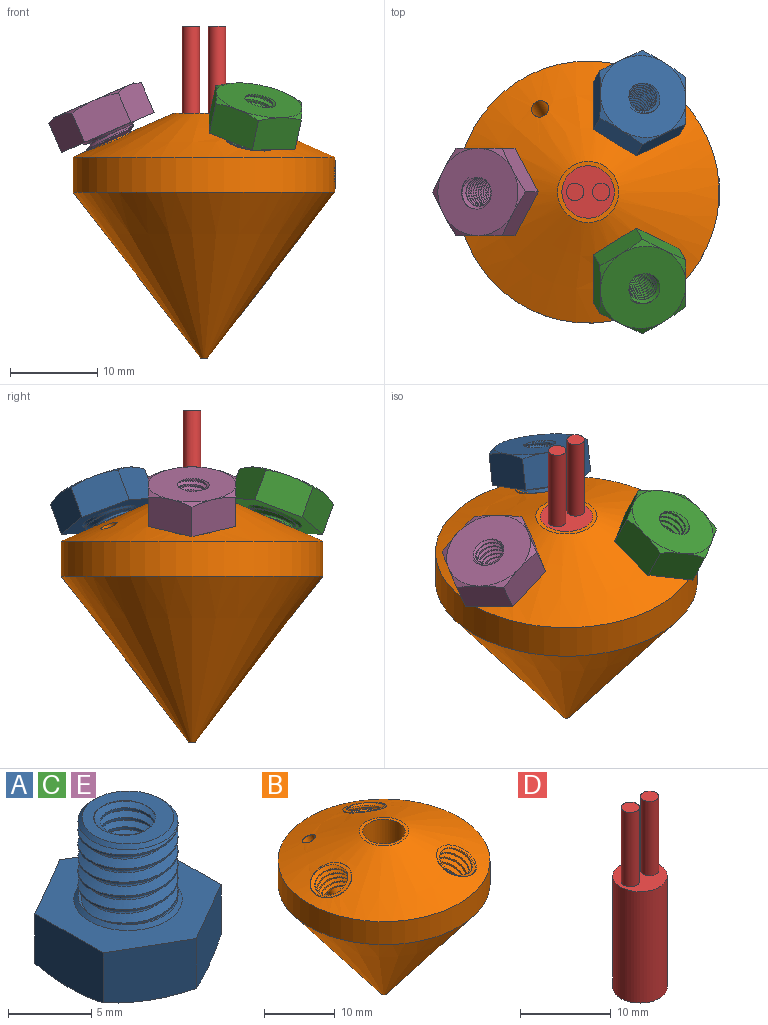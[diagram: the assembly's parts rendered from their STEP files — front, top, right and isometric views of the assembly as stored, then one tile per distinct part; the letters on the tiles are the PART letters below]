
ASSEMBLY  parts=5 mates=4
PART A: 27 faces, bbox 12x12x11.1 mm
  f0: plane 6.23x4.45mm, normal (1,0,0), area 22.5mm2, adj f1,f5,f7,f12,f17
  f1: plane 5.45x4.45mm, normal (0.5,0.87,0), area 22.5mm2, adj f0,f2,f7,f12,f13
  f2: plane 5.45x4.45mm, normal (-0.5,0.87,0), area 22.5mm2, adj f1,f3,f7,f13,f14
  f3: plane 6.23x4.45mm, normal (-1,0,0), area 22.5mm2, adj f2,f4,f7,f14,f15
  f4: plane 5.45x4.45mm, normal (-0.5,-0.87,0), area 22.5mm2, adj f3,f5,f7,f15,f16
  f5: plane 5.45x4.45mm, normal (0.5,-0.87,0), area 22.5mm2, adj f0,f4,f7,f16,f17
  f6: plane 10.2x10.2mm, normal (0,0,-1), area 68.1mm2, adj f12,f13,f14,f15,f16,f17,f23,f24
  f7: plane 11.55x10mm, normal (0,0,1), area 53.4mm2, adj f0,f1,f2,f3,f4,f5,f10
  f8: cylinder r=3mm len=6mm, axis (0,0,-1), area 11.3mm2, adj f10,f11,f19,f20
  f9: plane 5.69x5.69mm, normal (0,0,1), area 13.3mm2, adj f11,f23,f24,f25,f26
  f10: cone r=3mm half-angle=45deg, axis (0,0,-1), area 6.9mm2, adj f7,f8,f22
  f11: cone r=2.75mm half-angle=45deg, axis (0,0,-1), area 6.4mm2, adj f8,f9,f21
  f12: sphere r=13.56mm, area 2.3mm2, adj f0,f1,f6
  f13: sphere r=13.56mm, area 2.3mm2, adj f1,f2,f6
  f14: sphere r=13.56mm, area 2.3mm2, adj f2,f3,f6
  f15: sphere r=13.56mm, area 2.3mm2, adj f3,f4,f6
  f16: sphere r=13.56mm, area 2.3mm2, adj f4,f5,f6
  f17: sphere r=13.56mm, area 2.3mm2, adj f0,f5,f6
  f18: bspline ~6.25x5.68mm, area 23.5mm2, adj f19,f20,f21,f22
  f19: bspline ~6.93x6.31mm, area 59.1mm2, adj f8,f18,f21,f22
  f20: bspline ~6.93x6.15mm, area 59.1mm2, adj f8,f18,f21,f22
  f21: plane 6.28x6.28mm, normal (0,0,-1), area 5.5mm2, adj f11,f18,f19,f20
  f22: plane 6.28x6.28mm, normal (0,0,1), area 5.5mm2, adj f10,f18,f19,f20
  f23: bspline ~10.49x4.69mm, area 72.3mm2, adj f6,f9,f25,f26
  f24: bspline ~10.6x4.69mm, area 72.4mm2, adj f6,f9,f25,f26
  f25: bspline ~10.24x4.76mm, area 18.5mm2, adj f6,f9,f23,f24
  f26: cylinder r=1.65mm len=10mm, axis (0,0,1), area 29mm2, adj f6,f9,f23,f24
PART B: 59 faces, bbox 30.7x30.3x28.3 mm
  f0: cone r=3.5mm half-angle=66.5deg, axis (0,0,-1), area 637.1mm2, adj f1,f7,f18,f22,f23,f25,f26,f30
  f1: cylinder r=15mm len=30mm, axis (0,0,-1), area 369.3mm2, adj f0,f8,f46,f48,f49,f50
  f2: cylinder r=3mm len=15mm, axis (0,0,1), area 274.9mm2, adj f7,f43,f46,f47,f51,f52,f54,f56
  f3: cylinder r=0.2mm len=2.75mm, axis (-0.4,0,0.92), area 3.2mm2, adj f4,f5,f11,f42
  f4: cylinder r=0.2mm len=2.75mm, axis (0.2,-0.35,0.92), area 3.2mm2, adj f3,f5,f14,f42
  f5: cylinder r=0.2mm len=2.75mm, axis (0.2,0.35,0.92), area 3.2mm2, adj f3,f4,f17,f42
  f6: plane 0.8x0.8mm, normal (0,0,-1), area 0.4mm2, adj f8,f42
  f7: plane 7x7mm, normal (0,0,1), area 10.2mm2, adj f0,f2
  f8: cone r=15mm half-angle=37.5deg, axis (0,0,1), area 1159.3mm2, adj f1,f6
  f9: cone r=1mm half-angle=90deg, axis (-0.4,0,0.92), area 474.1mm2, adj f10,f27,f28,f29,f32
  f10: cylinder r=1mm len=17.27mm, axis (-0.4,0,0.92), area 112.9mm2, adj f9,f11
  f11: cone r=0.2mm half-angle=45deg, axis (-0.4,0,0.92), area 4.3mm2, adj f3,f10
  f12: cone r=1mm half-angle=90deg, axis (0.2,-0.35,0.92), area 474.1mm2, adj f13,f35,f36,f37,f41
  f13: cylinder r=1mm len=17.27mm, axis (0.2,-0.35,0.92), area 112.9mm2, adj f12,f14
  f14: cone r=0.2mm half-angle=45deg, axis (0.2,-0.35,0.92), area 4.3mm2, adj f4,f13
  f15: cone r=1mm half-angle=90deg, axis (0.2,0.35,0.92), area 474.1mm2, adj f16,f19,f20,f21,f24
  f16: cylinder r=1mm len=17.27mm, axis (0.2,0.35,0.92), area 112.9mm2, adj f15,f17
  f17: cone r=0.2mm half-angle=45deg, axis (0.2,0.35,0.92), area 4.3mm2, adj f5,f16
  f18: bspline ~7.91x7.08mm, area 13.7mm2, adj f0,f19,f20,f21,f22,f23,f25
  f19: bspline ~8.14x7.1mm, area 54.4mm2, adj f15,f18,f21,f24,f25
  f20: bspline ~8.14x6.98mm, area 54.5mm2, adj f15,f18,f21,f24,f25
  f21: plane 2.9x1.07mm, normal (0.2,0.35,0.92), area 0.2mm2, adj f15,f18,f19,f20
  f22: cylinder r=3.06mm len=4.21mm, axis (-0.2,-0.35,-0.92), area 0.1mm2, adj f0,f18,f25
  f23: cylinder r=3.06mm len=6.03mm, axis (-0.2,-0.35,-0.92), area 1.3mm2, adj f0,f18,f25
  f24: cylinder r=2.5mm len=6.58mm, axis (-0.2,-0.35,-0.92), area 19mm2, adj f15,f19,f20,f25
  f25: plane 6.29x6.04mm, normal (0.2,0.35,0.92), area 5.8mm2, adj f0,f18,f19,f20,f22,f23,f24
  f26: bspline ~7.51x7.13mm, area 13.7mm2, adj f0,f27,f28,f29,f30,f31,f33
  f27: bspline ~7.44x7.02mm, area 54.4mm2, adj f9,f26,f29,f32,f33
  f28: bspline ~7.44x7.02mm, area 54.5mm2, adj f9,f26,f29,f32,f33
  f29: plane 2.23x2.08mm, normal (-0.4,0,0.92), area 0.2mm2, adj f9,f26,f27,f28
  f30: cylinder r=3.06mm len=3.1mm, axis (0.4,0,-0.92), area 0.1mm2, adj f0,f26,f33
  f31: cylinder r=3.06mm len=6.13mm, axis (0.4,0,-0.92), area 0.5mm2, adj f0,f26,f33
  f32: cylinder r=2.5mm len=6.58mm, axis (0.4,0,-0.92), area 19mm2, adj f9,f27,f28,f33
  f33: plane 6.41x5.91mm, normal (-0.4,0,0.92), area 5.8mm2, adj f0,f26,f27,f28,f30,f31,f32
  f34: bspline ~8.26x7.08mm, area 13.7mm2, adj f0,f35,f36,f37,f38,f39,f40
  f35: bspline ~8.14x6.98mm, area 54.4mm2, adj f12,f34,f37,f38,f41
  f36: bspline ~8.14x6.98mm, area 54.5mm2, adj f12,f34,f37,f38,f41
  f37: plane 2.95x0.94mm, normal (0.2,-0.35,0.92), area 0.2mm2, adj f12,f34,f35,f36
  f38: plane 6.29x6.04mm, normal (0.2,-0.35,0.92), area 5.8mm2, adj f0,f34,f35,f36,f39,f40,f41
  f39: cylinder r=3.06mm len=6.03mm, axis (-0.2,0.35,-0.92), area 1.3mm2, adj f0,f34,f38
  f40: cylinder r=3.06mm len=4.18mm, axis (-0.2,0.35,-0.92), area 0.1mm2, adj f0,f34,f38
  f41: cylinder r=2.5mm len=6.58mm, axis (-0.2,0.35,-0.92), area 19mm2, adj f12,f35,f36,f38
  f42: cylinder r=0.2mm len=0.48mm, axis (0,0,-1), area 0.6mm2, adj f3,f4,f5,f6
  f43: cone r=0mm half-angle=59deg, axis (0,0,1), area 33mm2, adj f2
  f44: bspline ~13.15x3.56mm, area 62.2mm2, adj f46,f53,f55,f56
  f45: bspline ~13.15x3.56mm, area 62.1mm2, adj f46,f53,f55,f56
  f46: bspline ~12.79x3.66mm, area 17.5mm2, adj f1,f2,f44,f45,f47,f48,f50,f51
  f47: plane 0.84x0.09mm, normal (1,0,0), area 0mm2, adj f2,f46
  f48: cylinder r=1.56mm len=0.81mm, axis (-1,0,0), area 0mm2, adj f1,f46,f55
  f49: cylinder r=1.56mm len=3.13mm, axis (-1,0,0), area 0mm2, adj f1,f55
  f50: cylinder r=1.56mm len=2.67mm, axis (-1,0,0), area 0.1mm2, adj f1,f46,f55
  f51: cylinder r=1.56mm len=1.57mm, axis (-1,0,0), area 0.1mm2, adj f2,f46
  f52: cylinder r=1.56mm len=3mm, axis (-1,0,0), area 0.7mm2, adj f2,f46,f56
  f53: cylinder r=1mm len=12.4mm, axis (-1,0,0), area 21.5mm2, adj f44,f45,f55,f56
  f54: cylinder r=1.56mm len=2.98mm, axis (-1,0,0), area 0.8mm2, adj f2,f46,f56
  f55: plane 3.39x3.39mm, normal (1,0,0), area 2.7mm2, adj f44,f45,f46,f48,f49,f50,f53
  f56: plane 3.4x3.27mm, normal (-1,0,0), area 2.7mm2, adj f2,f44,f45,f46,f52,f53,f54
  f57: cylinder r=1mm len=9.92mm, axis (-0.2,0.35,0.92), area 62.5mm2, adj f0,f58
  f58: plane 1.96x1.88mm, normal (-0.2,0.35,0.92), area 3.1mm2, adj f57
PART C: same geometry as A
PART D: 7 faces, bbox 6x6x25 mm
  f0: cylinder r=3mm len=15mm, axis (0,0,-1), area 282.7mm2, adj f1,f2
  f1: plane 6x6mm, normal (0,0,1), area 22mm2, adj f0,f3,f5
  f2: plane 6x6mm, normal (0,0,-1), area 28.3mm2, adj f0
  f3: cylinder r=1mm len=10mm, axis (0,0,-1), area 62.8mm2, adj f1,f4
  f4: plane 2x2mm, normal (0,0,1), area 3.1mm2, adj f3
  f5: cylinder r=1mm len=10mm, axis (0,0,-1), area 62.8mm2, adj f1,f6
  f6: plane 2x2mm, normal (0,0,1), area 3.1mm2, adj f5
PART E: same geometry as A
PLACE A rot(axis=(0.99,-0.02,-0.1),159.5deg) t=(-26.8,-0.43,21.96)mm
PLACE B t=(-33.1,-11.35,-7.53)mm fixed
PLACE C rot(axis=(-0.99,-0.02,0.1),159.5deg) t=(-26.8,-22.27,21.96)mm
PLACE D t=(-33.1,-11.35,5.47)mm
PLACE E rot(axis=(-0.7,0.7,-0.15),163.4deg) t=(-45.71,-11.35,21.96)mm
MATE fastened A.f8 <-> B.f17  axis (-0.2,-0.35,-0.92) through (-28.79,-3.89,12.79)mm
MATE fastened C.f8 <-> B.f14  axis (-0.2,0.35,-0.92) through (-28.79,-18.81,12.79)mm
MATE fastened E.f8 <-> B.f3  axis (0.4,0,-0.92) through (-41.72,-11.35,12.79)mm
MATE fastened D.f0 <-> B.f0  axis (0,0,-1) through (-33.1,-11.35,5.47)mm
